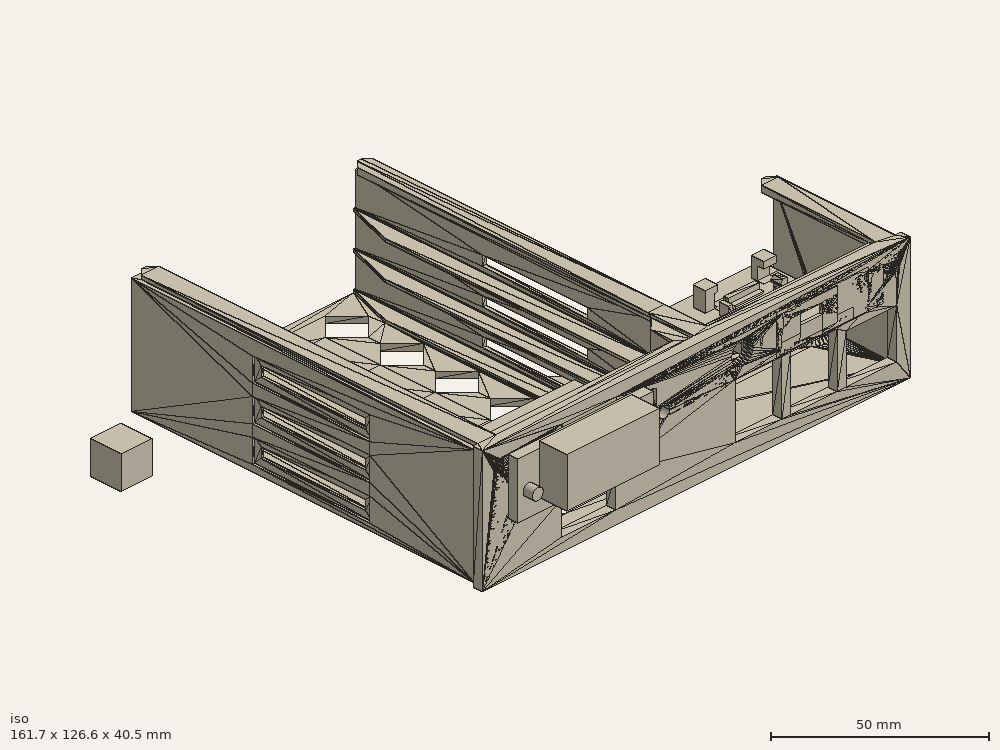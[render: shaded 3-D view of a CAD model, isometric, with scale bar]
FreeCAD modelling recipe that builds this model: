
FCSTD DOCUMENT  (FreeCAD 0.19R24291 (Git))
Label: trpi4-1
License: All rights reserved
LicenseURL: http://en.wikipedia.org/wiki/All_rights_reserved
objects: Part::Box×26, Part::MultiFuse×11, Part::Cut×8, Part::Cylinder×4, Part::Feature×3, Part::Chamfer×2
note: 54 computed .brp shape members not serialized (recipe doc carries the construction recipe); baked Part::Feature solids carry a one-line shape summary decoded from their .brp

FEATURE [Part::Box] Box  label="Cube"
  AttacherType = Attacher::AttachEngine3D
  Height = 10
  Length = 18
  Placement = pos=(48,-95,27) rot=(0,0,1;0rad)
  Width = 3
FEATURE [Part::Feature] tpi4001
  shape: bbox 139.2 x 114.6 x 37.45 mm, 2746 faces, 0 solids (baked)
FEATURE [Part::Feature] tpi4001_solid  label="tpi4001 (Solid)"
  shape: bbox 139.2 x 114.6 x 37.45 mm, 2746 faces (baked)
FEATURE [Part::MultiFuse] Fusion
  Shapes = -> [tpi4001_solid,Box]
FEATURE [Part::Box] Box006  label="Cube006"
  AttacherType = Attacher::AttachEngine3D
  Height = 5
  Length = 19
  Placement = pos=(7,1,0) rot=(0,0,1;0rad)
  Width = 4
FEATURE [Part::Box] Box003  label="Cube003"
  AttacherType = Attacher::AttachEngine3D
  Height = 10
  Length = 12
  Placement = pos=(13,-4,1) rot=(0,0,1;0rad)
  Width = 7
FEATURE [Part::Box] Box004  label="Cube004"
  AttacherType = Attacher::AttachEngine3D
  Height = 6
  Length = 4
  Placement = pos=(23,22,3) rot=(0,0,1;0rad)
  Width = 4
FEATURE [Part::Box] Box005  label="Cube005"
  AttacherType = Attacher::AttachEngine3D
  Height = 6
  Length = 4
  Placement = pos=(4,22,3) rot=(0,0,1;0rad)
  Width = 4
FEATURE [Part::Box] Box001  label="Cube001"
  AttacherType = Attacher::AttachEngine3D
  Height = 12
  Length = 40
  Width = 3
FEATURE [Part::Box] Box002  label="Cube002"
  AttacherType = Attacher::AttachEngine3D
  Height = 4
  Length = 30.1
  Placement = pos=(7,1,3) rot=(0,0,1;0rad)
  Width = 23.1
FEATURE [Part::Box] Box007  label="Cube007"
  AttacherType = Attacher::AttachEngine3D
  Height = 6
  Length = 7
  Placement = pos=(25,1,3) rot=(0,0,1;0rad)
  Width = 4
FEATURE [Part::Box] Box008  label="Cube008"
  AttacherType = Attacher::AttachEngine3D
  Height = 3
  Length = 30
  Width = 30
FEATURE [Part::MultiFuse] Fusion001
  Shapes = -> [Box008,Box001,Box004,Box005]
FEATURE [Part::Cut] Cut
  Base = -> Fusion001
  Tool = -> Box003
FEATURE [Part::Cut] Cut001
  Base = -> Cut
  Tool = -> Box002
FEATURE [Part::MultiFuse] Fusion002
  Shapes = -> [Box006,Cut001]
FEATURE [Part::Cut] Cut002  label="ttl-usb-ver1"
  Base = -> Fusion002
  Placement = pos=(113,-95,26.4) rot=(0,0,1;0rad)
  Tool = -> Box007
FEATURE [Part::Box] Box009  label="Cube009"
  AttacherType = Attacher::AttachEngine3D
  Height = 17
  Length = 44
  Placement = pos=(36,-98,19) rot=(0,0,1;0rad)
  Width = 3
FEATURE [Part::Box] Box010  label="Cube010"
  AttacherType = Attacher::AttachEngine3D
  Height = 15
  Length = 30
  Placement = pos=(43,-107,23) rot=(0,0,1;0rad)
  Width = 9
FEATURE [Part::Cylinder] Cylinder
  Angle = 360
  AttacherType = Attacher::AttachEngine3D
  Height = 10
  Placement = pos=(40,-91,26.5) rot=(1,0,0;1.5708rad)
  Radius = 1.75
FEATURE [Part::Cylinder] Cylinder001
  Angle = 360
  AttacherType = Attacher::AttachEngine3D
  Height = 10
  Placement = pos=(76.5,-91,26.5) rot=(1,0,0;1.5708rad)
  Radius = 1.75
FEATURE [Part::Box] Box011  label="Cube011"
  AttacherType = Attacher::AttachEngine3D
  Height = 12
  Length = 31.5
  Placement = pos=(42,-95,22) rot=(0,0,1;0rad)
  Width = 16
FEATURE [Part::MultiFuse] Fusion003
  Placement = pos=(-0.5,0,0) rot=(0,0,1;0rad)
  Shapes = -> [Cylinder001,Cylinder]
FEATURE [Part::MultiFuse] Fusion004  label="4P"
  Placement = pos=(-5,0,0) rot=(0,0,1;0rad)
  Shapes = -> [Box009,Box010,Box011,Fusion003]
FEATURE [Part::Box] Box013  label="Cube013"
  AttacherType = Attacher::AttachEngine3D
  Height = 12
  Length = 42.2
  Placement = pos=(5.97,-10,0.8) rot=(0,0,1;0rad)
  Width = 9
FEATURE [Part::Cylinder] Cylinder002
  Angle = 360
  AttacherType = Attacher::AttachEngine3D
  Height = 10
  Placement = pos=(47.15,0,0) rot=(1,0,0;1.5708rad)
  Radius = 1.75
FEATURE [Part::Cylinder] Cylinder003
  Angle = 360
  AttacherType = Attacher::AttachEngine3D
  Height = 10
  Placement = pos=(0,0,0) rot=(1,0,0;1.5708rad)
  Radius = 1.75
FEATURE [Part::MultiFuse] Fusion005
  Placement = pos=(3.5,0,5.5) rot=(0,0,1;0rad)
  Shapes = -> [Cylinder003,Cylinder002]
FEATURE [Part::MultiFuse] Fusion006  label="6P"
  Placement = pos=(31,-91,21.2) rot=(0,0,1;0rad)
  Shapes = -> [Box013,Fusion005]
FEATURE [Part::Cut] Cut003  label="rpi4-tray"
  Base = -> Fusion
  Tool = -> Fusion006
FEATURE [Part::Box] Box014  label="Cube014"
  AttacherType = Attacher::AttachEngine3D
  Height = 5.5
  Length = 3
  Placement = pos=(-3,3,-3.5) rot=(0,0,1;0rad)
  Width = 10
  expr: .Placement.Base.z = -3.5
FEATURE [Part::Box] Box015  label="Cube015"
  AttacherType = Attacher::AttachEngine3D
  Height = 2
  Length = 21
  Placement = pos=(-3,-2,-3.5) rot=(0,0,1;0rad)
  Width = 20
FEATURE [Part::Box] Box016  label="Cube016"
  AttacherType = Attacher::AttachEngine3D
  Height = 5.5
  Length = 3
  Placement = pos=(16,3,-3.5) rot=(0,0,1;0rad)
  Width = 10
  expr: .Placement.Base.z = -3.5
FEATURE [Part::Box] Box017  label="Cube017"
  AttacherType = Attacher::AttachEngine3D
  Height = 3
  Length = 2
  Placement = pos=(18,3,2) rot=(0,0,1;0rad)
  Width = 10
FEATURE [Part::Box] Box018  label="Cube018"
  AttacherType = Attacher::AttachEngine3D
  Height = 7
  Length = 3
  Placement = pos=(0,0,-5) rot=(0,0,1;0rad)
  Width = 16
FEATURE [Part::Box] Box019  label="ttl-usb-board"
  AttacherType = Attacher::AttachEngine3D
  Height = 1.6
  Length = 19.5
  Placement = pos=(-1.5,0,0.4) rot=(0,0,1;0rad)
  Width = 16
FEATURE [Part::Box] Box020  label="Cube020"
  AttacherType = Attacher::AttachEngine3D
  Height = 10
  Length = 3
  Placement = pos=(0,0.75,-3) rot=(0,0,1;0rad)
  Width = 14.5
FEATURE [Part::Box] Box021  label="Cube021"
  AttacherType = Attacher::AttachEngine3D
  Height = 12
  Length = 1
  Placement = pos=(18,-2,-3.5) rot=(0,0,1;0rad)
  Width = 30
FEATURE [Part::MultiFuse] Fusion008
  Shapes = -> [Box018,Box020]
FEATURE [Part::Cut] Cut006
  Base = -> Box021
  Tool = -> Box017
FEATURE [Part::Box] Box022  label="Cube022"
  AttacherType = Attacher::AttachEngine3D
  Height = 7
  Length = 3
  Placement = pos=(0,-1.5,-3.5) rot=(0,0,1;0rad)
  Width = 19
FEATURE [Part::Cut] Cut004
  Base = -> Box022
  Tool = -> Fusion008
FEATURE [Part::Chamfer] Chamfer
  Base = -> Cut004
  Edges = 2 edges r=1: [Edge7,Edge27]
FEATURE [Part::Box] Box023  label="Cube023"
  AttacherType = Attacher::AttachEngine3D
  Height = 10
  Length = 10
  Width = 10
FEATURE [Part::Feature] Fusion009_solid  label="rpi4-tray-all (Solid)"
  shape: bbox 139.2 x 114.6 x 37.45 mm, 2884 faces (baked)
FEATURE [Part::Box] Box024  label="Cube024"
  AttacherType = Attacher::AttachEngine3D
  Height = 7
  Length = 3
  Placement = pos=(0,0,-5) rot=(0,0,1;0rad)
  Width = 16
FEATURE [Part::Box] Box025  label="Cube025"
  AttacherType = Attacher::AttachEngine3D
  Height = 10
  Length = 3
  Placement = pos=(0,0.75,-3) rot=(0,0,1;0rad)
  Width = 14.5
FEATURE [Part::MultiFuse] Fusion010
  Shapes = -> [Box024,Box025]
FEATURE [Part::Box] Box026  label="Cube026"
  AttacherType = Attacher::AttachEngine3D
  Height = 7
  Length = 3
  Placement = pos=(0,-1.5,-3.5) rot=(0,0,1;0rad)
  Width = 19
FEATURE [Part::Cut] Cut007
  Base = -> Box026
  Tool = -> Fusion010
FEATURE [Part::Chamfer] Chamfer001
  Base = -> Cut007
  Edges = 2 edges r=1: [Edge7,Edge27]
  Placement = pos=(12,0,0) rot=(0,0,1;0rad)
FEATURE [Part::MultiFuse] Fusion007
  Shapes = -> [Box014,Box015,Chamfer,Cut006,Box016,Chamfer001]
FEATURE [Part::Cut] Cut005  label="ttl-usb-ver2"
  Base = -> Fusion007
  Placement = pos=(120,-76,29.55) rot=(0,0,-1;1.5708rad)
  Tool = -> Box019
FEATURE [Part::MultiFuse] Fusion009  label="rpi4-tray-all"
  Shapes = -> [Cut005,Cut003]
